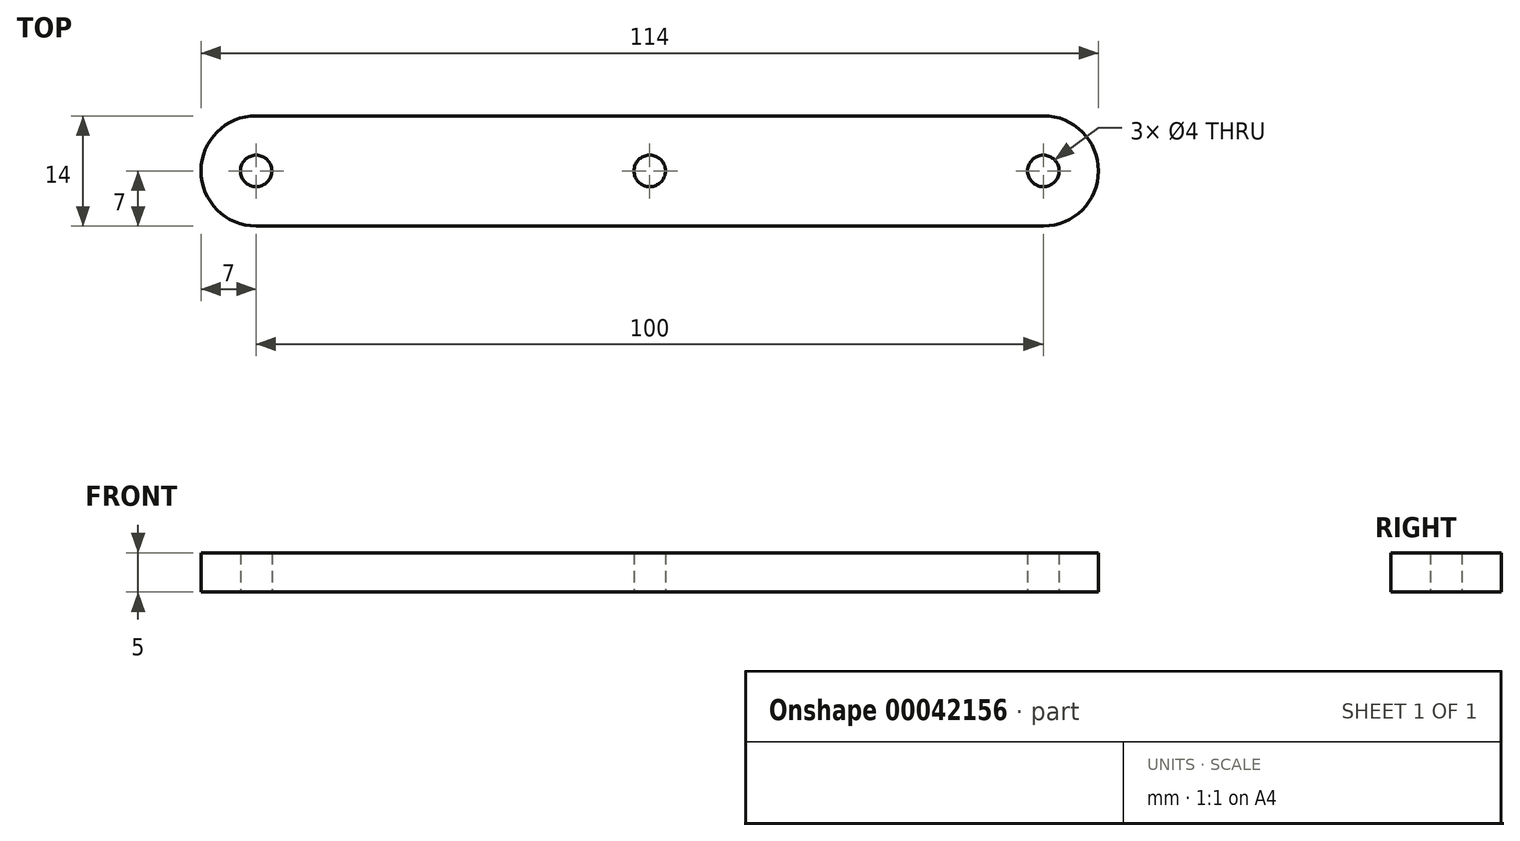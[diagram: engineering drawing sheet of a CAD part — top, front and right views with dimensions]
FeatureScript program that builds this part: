
annotation { "Feature Type Name" : "Feature", "Feature Type Description" : "" }
export const myFeature = defineFeature(function(context is Context, id is Id, definition is map)
    precondition{}
    {
        {
            var Q0;
            Q0=qCreatedBy(makeId("Top.planeOp"),FACE);
            var sketch = newSketch(context, id + "F0", { "sketchPlane" : qUnion([Q0])});
            skCircle(sketch, "E0", {"center": v(0, 0) * mm, "radius": 2 * mm});
            skCircle(sketch, "E1", {"center": v(-50, 0) * mm, "radius": 2 * mm});
            skCircle(sketch, "E2", {"center": v(-100, 0) * mm, "radius": 2 * mm});
            skLineSegment(sketch, "E3", {"start": v(0, 7) * mm, "end": v(-100, 7) * mm});
            skLineSegment(sketch, "E4", {"start": v(-100, -7) * mm, "end": v(0, -7) * mm});
            skArc(sketch, "E5", {"start": v(-100, 7) * mm, "mid": v(-107, 0) * mm, "end": v(-100, -7) * mm});
            skArc(sketch, "E6", {"start": v(0, 7) * mm, "mid": v(7, 0) * mm, "end": v(0, -7) * mm});
            skSolve(sketch);
        }
        {
            var Q0;
            Q0=makeQuery(id+"F0.imprint","IMPRINT",FACE,{"disambiguationData":[TD([[makeQuery(id+"F0.imprint","IMPRINT",EDGE,{"derivedFrom":sQuery(id+"F0.wireOp",EDGE,"E0")}),-1.0]])]});
            extrude(context, id + "F1", {"entities" : qUnion([Q0]), "depth" : 5 * mm});
        }
    });
